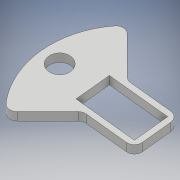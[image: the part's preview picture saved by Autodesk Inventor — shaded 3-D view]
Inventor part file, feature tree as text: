
AUTODESK INVENTOR PART (.ipt)
format: ipt  version: 2018 (Build 220112000, 112)  size: 133,120 bytes
history: native  units: mm
features: extrude x1, sketch x1
ambient origin geometry x8: Origin, YZ Plane, XZ Plane, XY Plane, X Axis, Y Axis, Z Axis, Center Point
bodies: Solid1 (feature_tree)
feature tree (2):
  extrude  "Extrusion1"  Depth=2.0mm
  sketch  "Sketch1"  dims[d0=22.1mm d1=44.0mm d2=135.0deg d3=5.6mm d4=17.25mm d6=15.62706mm d14=2.4mm d15=0.0mm d16=1.0mm d18=2.0mm d19=1.0mm d20=2.0mm d21=2.0mm d22=45.0deg d23=14.9mm d24=2.0mm]
